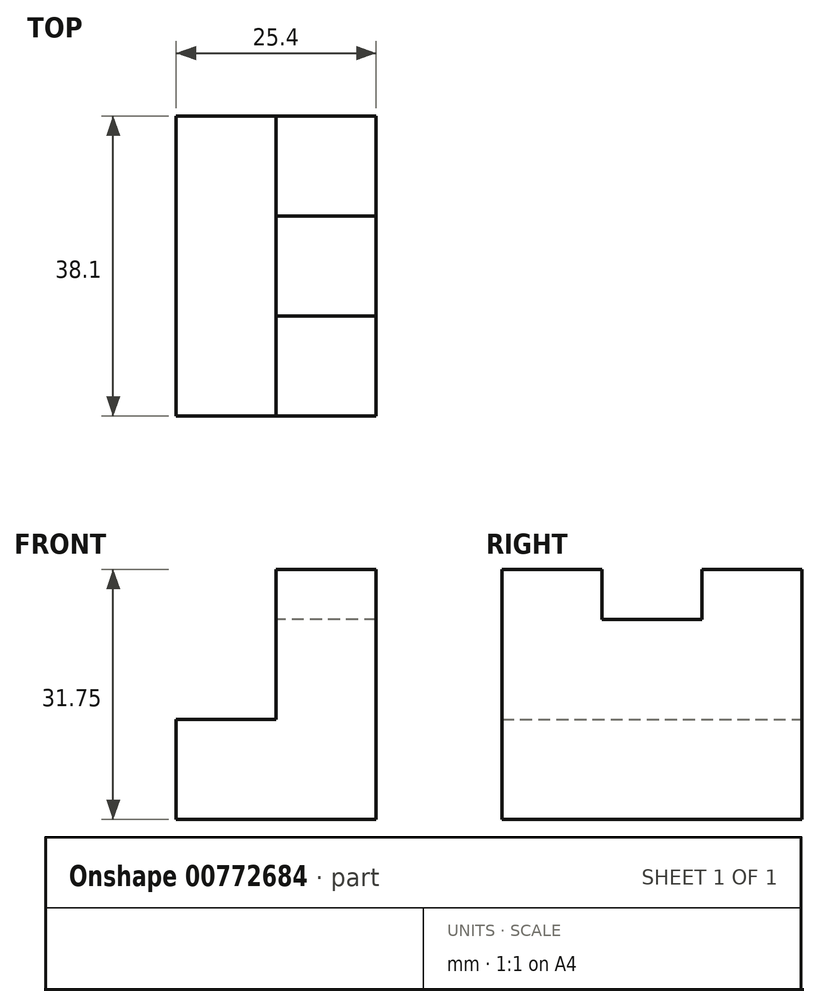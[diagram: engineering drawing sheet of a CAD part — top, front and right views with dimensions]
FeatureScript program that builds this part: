
annotation { "Feature Type Name" : "Feature", "Feature Type Description" : "" }
export const myFeature = defineFeature(function(context is Context, id is Id, definition is map)
    precondition{}
    {
        {
            var Q0;
            Q0=qCreatedBy(makeId("Front.planeOp"),FACE);
            var sketch = newSketch(context, id + "F0", { "sketchPlane" : qUnion([Q0])});
            skLineSegment(sketch, "E0", {"start": v(0, 0) * mm, "end": v(0, 31.75) * mm});
            skLineSegment(sketch, "E1", {"start": v(0, 0) * mm, "end": v(-25.4, 0) * mm});
            skLineSegment(sketch, "E2", {"start": v(-25.4, 0) * mm, "end": v(-25.4, 12.7) * mm});
            skLineSegment(sketch, "E3", {"start": v(-25.4, 12.7) * mm, "end": v(-12.7, 12.7) * mm});
            skLineSegment(sketch, "E4", {"start": v(-12.7, 12.7) * mm, "end": v(-12.7, 31.75) * mm});
            skLineSegment(sketch, "E5", {"start": v(-12.7, 31.75) * mm, "end": v(0, 31.75) * mm});
            skSolve(sketch);
        }
        {
            var Q0;
            Q0=makeQuery(id+"F0.imprint","IMPRINT",FACE,{"disambiguationData":[TD([[makeQuery(id+"F0.imprint","IMPRINT",EDGE,{"derivedFrom":sQuery(id+"F0.wireOp",EDGE,"E0")}),1.0]])]});
            extrude(context, id + "F1", {"entities" : qUnion([Q0]), "depth" : 38.1 * mm, "offsetDistance" : 25.4 * mm});
        }
        {
            var Q0;
            Q0=makeQuery(id+"F1.opExtrude","SWEPT_FACE",FACE,{"disambiguationData":[OSD([sQuery(id+"F0.wireOp",EDGE,"E4")])]});
            var sketch = newSketch(context, id + "F2", { "sketchPlane" : qUnion([Q0])});
            skLineSegment(sketch, "E6", {"start": v(38.1, 31.75) * mm, "end": v(38.1, 31.75) * mm});
            skLineSegment(sketch, "E7", {"start": v(38.1, 31.75) * mm, "end": v(25.4, 31.75) * mm});
            skLineSegment(sketch, "E8", {"start": v(0, 31.75) * mm, "end": v(12.7, 31.75) * mm});
            skLineSegment(sketch, "E9", {"start": v(12.7, 31.75) * mm, "end": v(12.7, 25.4) * mm});
            skLineSegment(sketch, "E10", {"start": v(25.4, 31.75) * mm, "end": v(25.4, 25.4) * mm});
            skLineSegment(sketch, "E11", {"start": v(12.7, 25.4) * mm, "end": v(25.4, 25.4) * mm});
            skSolve(sketch);
        }
        {
            var Q0;
            {var subQ0=sQuery(id+"F2.wireOp",EDGE,"E9");Q0=makeQuery(id+"F2.imprint","IMPRINT",FACE,{"disambiguationData":[TD([[makeQuery(id+"F2.imprint","IMPRINT",EDGE,{"derivedFrom":subQ0}),1.0]])]});}
            extrude(context, id + "F3", {"entities" : qUnion([Q0]), "operationType" : NewBodyOperationType.REMOVE, "oppositeDirection" : true, "depth" : 12.7 * mm, "offsetDistance" : 25.4 * mm});
        }
    });
